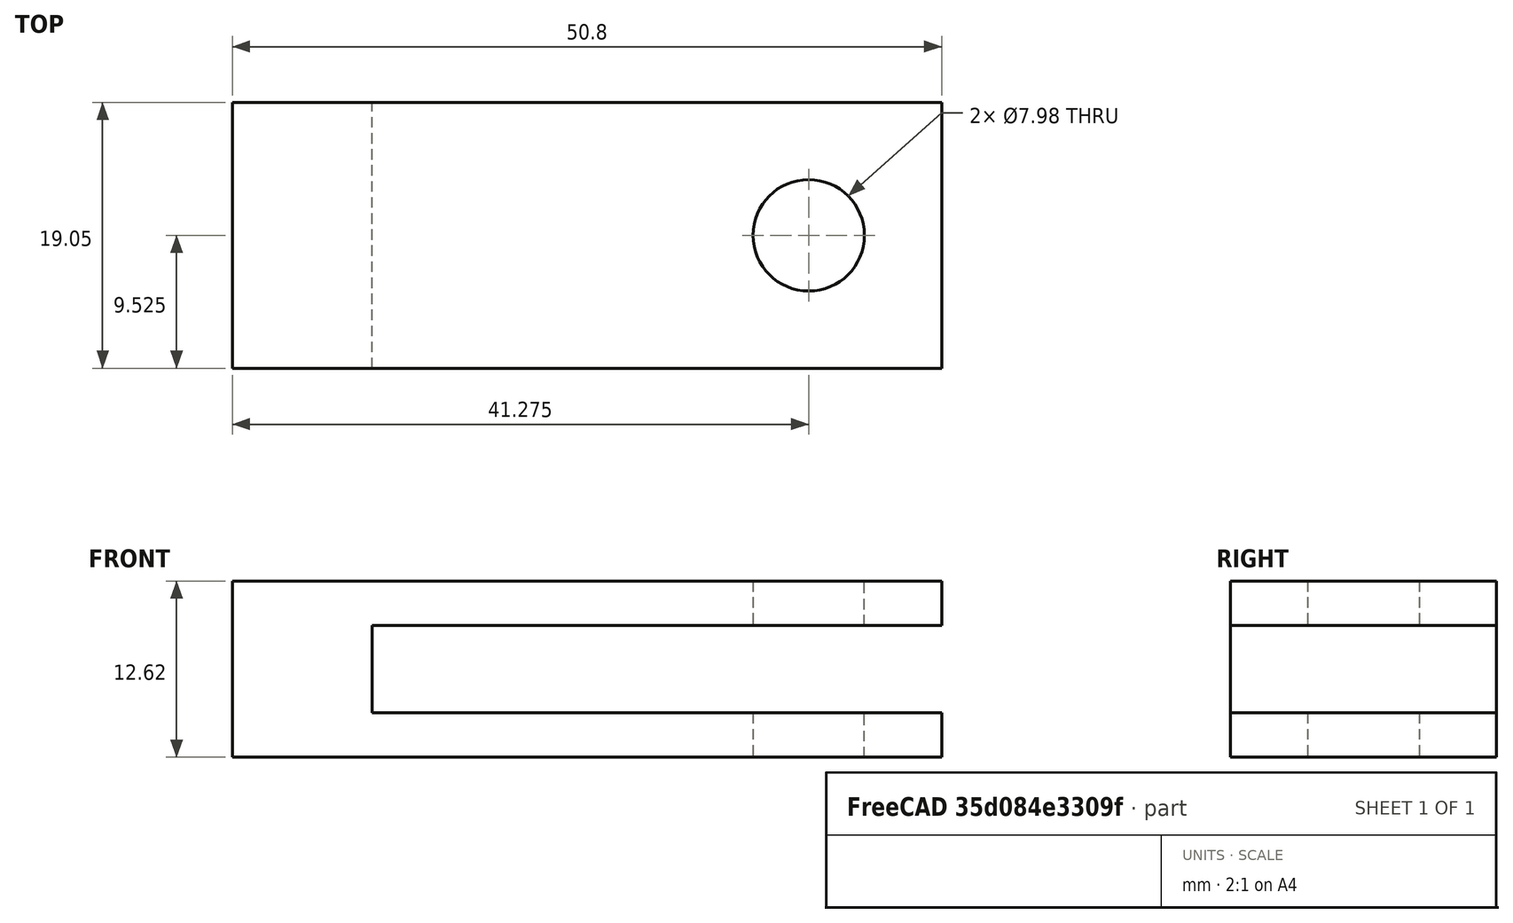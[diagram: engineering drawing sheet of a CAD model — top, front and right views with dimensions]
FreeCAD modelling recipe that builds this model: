
FCSTD DOCUMENT  (FreeCAD 0.21R33771 (Git))
Label: boot stuff
License: All rights reserved
LicenseURL: http://en.wikipedia.org/wiki/All_rights_reserved
objects: Part::Box×3, Part::MultiFuse×1, Part::Cylinder×1, Part::Cut×1, App::Part×1
note: 6 computed .brp shape members not serialized (recipe doc carries the construction recipe); baked Part::Feature solids carry a one-line shape summary decoded from their .brp

FEATURE [Part::Box] Box  label="Cube"
  AttacherType = Attacher::AttachEngine3D
  Height = 3.175
  Length = 50.8
  Placement = pos=(0,0,8.026) rot=(0,0,1;0rad)
  Width = 19.05
FEATURE [Part::Box] Box001  label="Cube001"
  AttacherType = Attacher::AttachEngine3D
  Height = 3.175
  Length = 50.8
  Placement = pos=(0,0,-1.422) rot=(0,0,1;0rad)
  Width = 19.05
FEATURE [Part::Box] Box002  label="Cube002"
  AttacherType = Attacher::AttachEngine3D
  Height = 6.35
  Length = 10.0076
  Placement = pos=(0,0,1.676) rot=(0,0,1;0rad)
  Width = 19.05
FEATURE [Part::MultiFuse] Fusion
  Shapes = -> [Box,Box001,Box002]
FEATURE [Part::Cylinder] Cylinder
  Angle = 360
  AttacherType = Attacher::AttachEngine3D
  FirstAngle = 0
  Height = 25.4
  Placement = pos=(41.275,9.525,-7.62) rot=(0,0,1;0rad)
  Radius = 3.9878
  SecondAngle = 0
FEATURE [Part::Cut] Cut
  Base = -> Fusion
  Tool = -> Cylinder
FEATURE [App::Part] Part
  Group = -> [Fusion,Box,Box001,Cylinder,Box002,Cut]
  Origin = -> Origin
